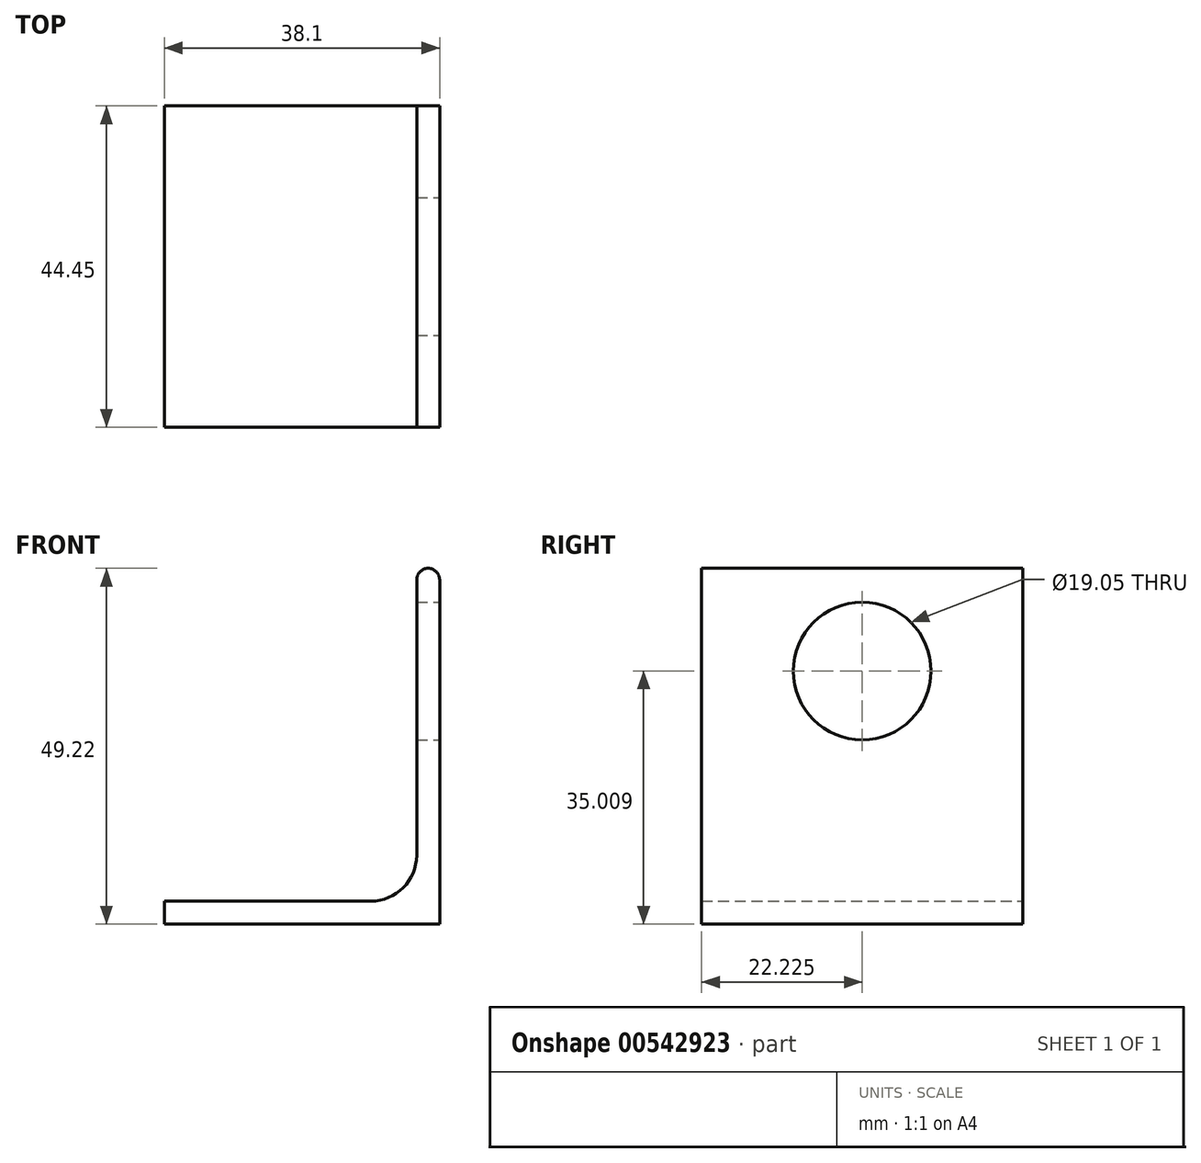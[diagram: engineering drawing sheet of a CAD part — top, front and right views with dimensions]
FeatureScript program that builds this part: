
annotation { "Feature Type Name" : "Feature", "Feature Type Description" : "" }
export const myFeature = defineFeature(function(context is Context, id is Id, definition is map)
    precondition{}
    {
        {
            var Q0;
            Q0=qCreatedBy(makeId("Front.planeOp"),FACE);
            var sketch = newSketch(context, id + "F0", { "sketchPlane" : qUnion([Q0])});
            skLineSegment(sketch, "E0", {"start": v(0, 0) * mm, "end": v(28.58, 0) * mm});
            skLineSegment(sketch, "E1", {"start": v(34.93, -3.18) * mm, "end": v(0, -3.18) * mm});
            skLineSegment(sketch, "E2", {"start": v(34.93, 6.35) * mm, "end": v(34.93, 44.45) * mm});
            skLineSegment(sketch, "E3", {"start": v(34.93, -3.18) * mm, "end": v(38.1, -3.18) * mm});
            skLineSegment(sketch, "E4", {"start": v(38.1, -3.18) * mm, "end": v(38.1, 44.45) * mm});
            skLineSegment(sketch, "E5", {"start": v(0, 0) * mm, "end": v(0, -3.18) * mm});
            skPoint(sketch, "E6.visualSharp", {"position": v(34.93, 0) * mm});
            skArc(sketch, "E6.filletArc", {"start": v(28.58, 0) * mm, "mid": v(33.07, 1.86) * mm, "end": v(34.93, 6.35) * mm});
            skArc(sketch, "E7", {"start": v(38.1, 44.45) * mm, "mid": v(36.51, 46.04) * mm, "end": v(34.93, 44.45) * mm});
            skSolve(sketch);
        }
        {
            var Q0;
            Q0=makeQuery(id+"F0.imprint","IMPRINT",FACE,{"disambiguationData":[TD([[makeQuery(id+"F0.imprint","IMPRINT",EDGE,{"derivedFrom":sQuery(id+"F0.wireOp",EDGE,"E0")}),-1.0]])]});
            extrude(context, id + "F1", {"entities" : qUnion([Q0]), "depth" : 44.45 * mm, "offsetDistance" : 25.4 * mm});
        }
        {
            var Q0;
            Q0=makeQuery(id+"F1.opExtrude","SWEPT_FACE",FACE,{"disambiguationData":[OSD([sQuery(id+"F0.wireOp",EDGE,"E4")])]});
            var sketch = newSketch(context, id + "F2", { "sketchPlane" : qUnion([Q0])});
            skPoint(sketch, "E8", {"position": v(-22.23, 31.83) * mm});
            skPoint(sketch, "E8.positionSnap0", {"position": v(-22.23, -3.18) * mm});
            skSolve(sketch);
        }
        {
            var Q0;
            Q0=sQuery(id+"F2.wireOp",VERTEX,"E8");
            var Q1;
            Q1=makeQuery(id+"F1.opExtrude","SWEPT_BODY",BODY,{"disambiguationData":[OSD([sQuery(id+"F0.wireOp",EDGE,"E0"),sQuery(id+"F0.wireOp",EDGE,"E1"),sQuery(id+"F0.wireOp",EDGE,"E2"),sQuery(id+"F0.wireOp",EDGE,"E3"),sQuery(id+"F0.wireOp",EDGE,"E4"),sQuery(id+"F0.wireOp",EDGE,"E5"),sQuery(id+"F0.wireOp",EDGE,"E6.filletArc"),sQuery(id+"F0.wireOp",EDGE,"E7")])]});
            hole(context, id + "F3", {"style" : HoleStyle.SIMPLE, "endStyle" : HoleEndStyle.BLIND, "holeDiameter" : 19.05 * mm, "majorDiameter" : 6.35 * mm, "holeDepth" : 25.4 * mm, "isTappedThrough" : true, "tappedDepth" : 12.7 * mm, "tapClearance" : 3, "locations" : qUnion([Q0]), "scope" : qUnion([Q1])});
        }
    });
